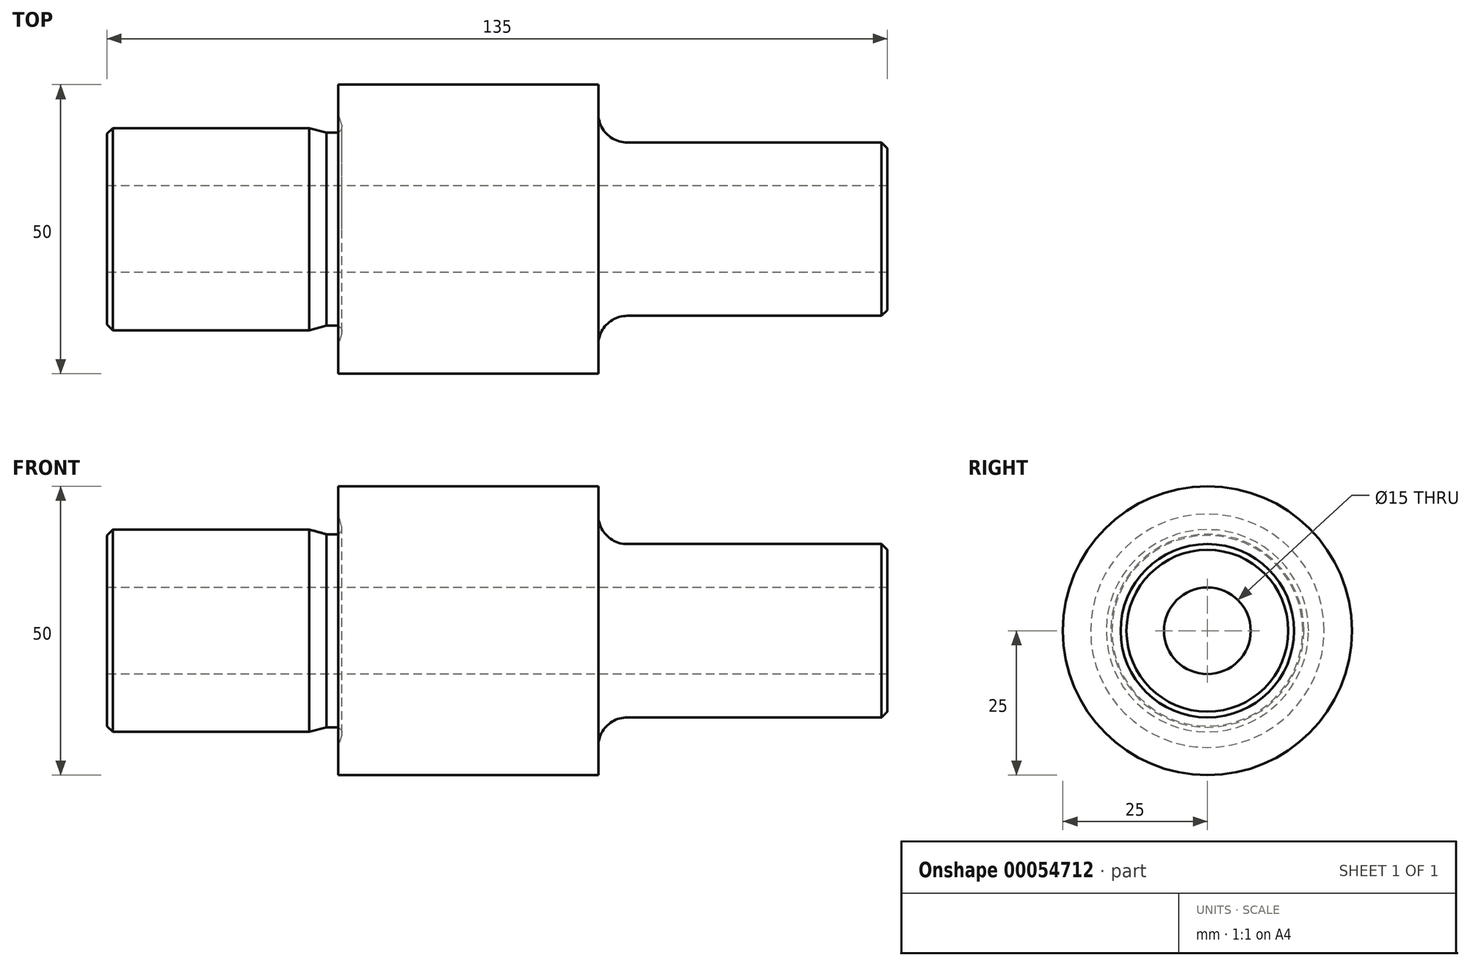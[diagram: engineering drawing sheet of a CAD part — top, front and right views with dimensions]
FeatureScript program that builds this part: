
annotation { "Feature Type Name" : "Feature", "Feature Type Description" : "" }
export const myFeature = defineFeature(function(context is Context, id is Id, definition is map)
    precondition{}
    {
        {
            var Q0;
            Q0=qCreatedBy(makeId("Front.planeOp"),FACE);
            var sketch = newSketch(context, id + "F0", { "sketchPlane" : qUnion([Q0])});
            skLineSegment(sketch, "E0", {"start": v(0, 7.5) * mm, "end": v(0, 17.5) * mm});
            skLineSegment(sketch, "E1", {"start": v(0, 17.5) * mm, "end": v(35, 17.5) * mm});
            skLineSegment(sketch, "E2", {"start": v(40, 20.2) * mm, "end": v(40, 25) * mm});
            skLineSegment(sketch, "E3", {"start": v(40, 25) * mm, "end": v(85, 25) * mm});
            skLineSegment(sketch, "E4", {"start": v(85, 25) * mm, "end": v(85, 15) * mm});
            skLineSegment(sketch, "E5", {"start": v(85, 15) * mm, "end": v(135, 15) * mm});
            skLineSegment(sketch, "E6", {"start": v(135, 15) * mm, "end": v(135, 7.5) * mm});
            skLineSegment(sketch, "E7", {"start": v(135, 7.5) * mm, "end": v(0, 7.5) * mm});
            skLineSegment(sketch, "E8.MirrorCS", {"start": v(135, -7.5) * mm, "end": v(0, -7.5) * mm, "construction": true});
            skLineSegment(sketch, "E9.MirrorCS", {"start": v(0, -7.5) * mm, "end": v(0, -17.5) * mm, "construction": true});
            skLineSegment(sketch, "E10.MirrorCS", {"start": v(0, -17.5) * mm, "end": v(40, -17.5) * mm, "construction": true});
            skLineSegment(sketch, "E11.MirrorCS", {"start": v(40, -17.5) * mm, "end": v(40, -25) * mm, "construction": true});
            skLineSegment(sketch, "E12.MirrorCS", {"start": v(40, -25) * mm, "end": v(85, -25) * mm, "construction": true});
            skLineSegment(sketch, "E13.MirrorCS", {"start": v(85, -25) * mm, "end": v(85, -15) * mm, "construction": true});
            skLineSegment(sketch, "E14.MirrorCS", {"start": v(85, -15) * mm, "end": v(135, -15) * mm, "construction": true});
            skLineSegment(sketch, "E15.MirrorCS", {"start": v(135, -15) * mm, "end": v(135, -7.5) * mm, "construction": true});
            skPoint(sketch, "E16.orphan", {"position": v(0, 0) * mm});
            skLineSegment(sketch, "E17", {"start": v(0, 0) * mm, "end": v(135, 0) * mm, "construction": true});
            skLineSegment(sketch, "E18", {"start": v(40, 20.2) * mm, "end": v(40.6, 17.96) * mm});
            skLineSegment(sketch, "E19", {"start": v(39.63, 16.7) * mm, "end": v(37.99, 16.7) * mm});
            skLineSegment(sketch, "E20", {"start": v(37.99, 16.7) * mm, "end": v(35, 17.5) * mm});
            skPoint(sketch, "E21.visualSharp", {"position": v(40.94, 16.7) * mm});
            skArc(sketch, "E21.filletArc", {"start": v(39.63, 16.7) * mm, "mid": v(40.43, 17.1) * mm, "end": v(40.6, 17.96) * mm});
            skPoint(sketch, "E22.orphan", {"position": v(40, 17.5) * mm});
            skSolve(sketch);
        }
        {
            var Q0;
            Q0=makeQuery(id+"F0.imprint","IMPRINT",FACE,{"disambiguationData":[TD([[makeQuery(id+"F0.imprint","IMPRINT",EDGE,{"derivedFrom":sQuery(id+"F0.wireOp",EDGE,"E0")}),-1.0]])]});
            var Q1;
            Q1=sQuery(id+"F0.wireOp",EDGE,"E17");
            revolve(context, id + "F1", {"entities" : qUnion([Q0]), "axis" : qUnion([Q1]), "revolveType" : RevolveType.FULL});
        }
        {
            var Q0;
            Q0=makeQuery(id+"F1.opRevolve","SWEPT_EDGE",EDGE,{"disambiguationData":[OSD([sQuery(id+"F0.wireOp",EDGE,"E0"),sQuery(id+"F0.wireOp",EDGE,"E1")])]});
            var Q1;
            Q1=makeQuery(id+"F1.opRevolve","SWEPT_EDGE",EDGE,{"disambiguationData":[OSD([sQuery(id+"F0.wireOp",EDGE,"E5"),sQuery(id+"F0.wireOp",EDGE,"E6")])]});
            chamfer(context, id + "F2", {"entities" : qUnion([Q0, Q1]), "width" : 1 * mm, "tangentPropagation" : true});
        }
        {
            var Q0;
            Q0=makeQuery(id+"F1.opRevolve","SWEPT_EDGE",EDGE,{"disambiguationData":[OSD([sQuery(id+"F0.wireOp",EDGE,"E4"),sQuery(id+"F0.wireOp",EDGE,"E5")])]});
            fillet(context, id + "F3", {"entities" : qUnion([Q0]), "radius" : 5 * mm, "tangentPropagation" : true, "allowEdgeOverflow" : false});
        }
    });
